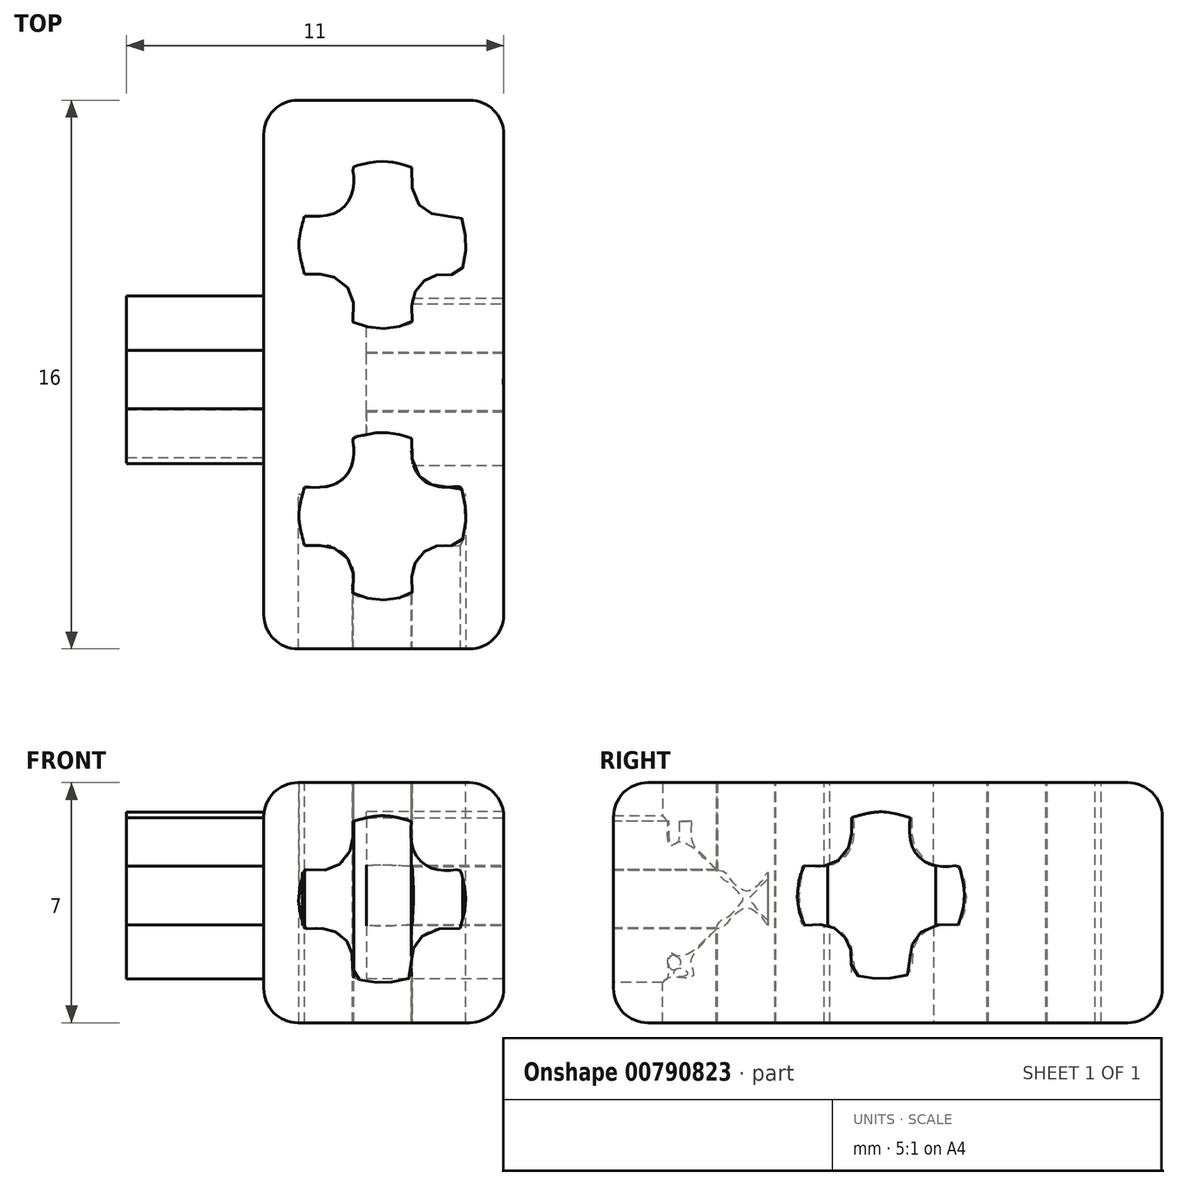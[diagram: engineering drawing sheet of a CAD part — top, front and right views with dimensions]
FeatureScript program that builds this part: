
annotation { "Feature Type Name" : "Feature", "Feature Type Description" : "" }
export const myFeature = defineFeature(function(context is Context, id is Id, definition is map)
    precondition{}
    {
        {
            var Q0;
            Q0=qCreatedBy(makeId("Top.planeOp"),FACE);
            var sketch = newSketch(context, id + "F0", { "sketchPlane" : qUnion([Q0])});
            skLineSegment(sketch, "E0.bottom", {"start": v(-3.5, 8) * mm, "end": v(3.5, 8) * mm});
            skLineSegment(sketch, "E0.top", {"start": v(-3.5, -8) * mm, "end": v(3.5, -8) * mm});
            skLineSegment(sketch, "E0.left", {"start": v(-3.5, 8) * mm, "end": v(-3.5, -8) * mm});
            skLineSegment(sketch, "E0.right", {"start": v(3.5, 8) * mm, "end": v(3.5, -8) * mm});
            skPoint(sketch, "E1", {"position": v(0, 8) * mm});
            skPoint(sketch, "E2", {"position": v(-3.5, 0) * mm});
            skSolve(sketch);
        }
        {
            var Q0;
            Q0=makeQuery(id+"F0.imprint","IMPRINT",FACE,{"disambiguationData":[TD([[makeQuery(id+"F0.imprint","IMPRINT",EDGE,{"derivedFrom":sQuery(id+"F0.wireOp",EDGE,"E0.bottom")}),-1.0]])]});
            extrude(context, id + "F1", {"entities" : qUnion([Q0]), "depth" : 7 * mm, "offsetDistance" : 25 * mm});
        }
        {
            var Q0;
            Q0=makeQuery(id+"F1.opExtrude","SWEPT_FACE",FACE,{"disambiguationData":[OSD([sQuery(id+"F0.wireOp",EDGE,"E0.left")])]});
            var sketch = newSketch(context, id + "F2", { "sketchPlane" : qUnion([Q0])});
            skFitSpline(sketch, "E3", {"points": [v(-0.7, 5.97) * mm, v(0.18, 6.14) * mm, v(1, 5.97) * mm], "startDerivative": vector(1.75, 0.5) * mm, "endDerivative": vector(1.65, -0.5) * mm});
            skFitSpline(sketch, "E4", {"points": [v(1, 5.97) * mm, v(1, 5.4) * mm, v(1.15, 4.97) * mm, v(1.46, 4.67) * mm, v(1.8, 4.56) * mm, v(2.22, 4.55) * mm, v(2.42, 4.55) * mm, v(2.5, 4.3) * mm, v(2.58, 3.92) * mm, v(2.59, 3.58) * mm, v(2.54, 3.26) * mm, v(2.42, 2.85) * mm], "startDerivative": vector(-0.26, -5.18) * mm, "endDerivative": vector(-1.41, -4.37) * mm});
            skFitSpline(sketch, "E5", {"points": [v(-0.7, 5.97) * mm, v(-0.7, 5.68) * mm, v(-0.7, 5.43) * mm, v(-0.73, 5.24) * mm, v(-0.9, 4.9) * mm, v(-1.1, 4.72) * mm, v(-1.36, 4.6) * mm, v(-1.68, 4.55) * mm, v(-2.12, 4.55) * mm, v(-2.21, 4.27) * mm, v(-2.27, 3.98) * mm, v(-2.29, 3.66) * mm, v(-2.26, 3.37) * mm, v(-2.2, 3.1) * mm, v(-2.12, 2.85) * mm, v(-1.93, 2.85) * mm, v(-1.61, 2.85) * mm, v(-1.36, 2.81) * mm, v(-1.17, 2.73) * mm, v(-0.95, 2.56) * mm, v(-0.84, 2.42) * mm, v(-0.76, 2.24) * mm, v(-0.7, 2) * mm, v(-0.7, 1.75) * mm, v(-0.7, 1.43) * mm, v(-0.44, 1.35) * mm, v(-0.1, 1.29) * mm, v(0.18, 1.28) * mm, v(0.45, 1.3) * mm, v(0.82, 1.37) * mm, v(1, 1.43) * mm, v(1, 1.75) * mm, v(1, 2.03) * mm, v(1.1, 2.35) * mm, v(1.24, 2.55) * mm, v(1.5, 2.75) * mm, v(1.92, 2.85) * mm, v(2.42, 2.85) * mm], "startDerivative": vector(-0.02, -10.87) * mm, "endDerivative": vector(14.17, -0.52) * mm});
            skSolve(sketch);
        }
        {
            var Q0;
            Q0=makeQuery(id+"F2.imprint","IMPRINT",FACE,{"disambiguationData":[TD([[makeQuery(id+"F2.imprint","IMPRINT",EDGE,{"derivedFrom":sQuery(id+"F2.wireOp",EDGE,"E3")}),-1.0]])]});
            var Q1;
            Q1=makeQuery(id+"F2.imprint","IMPRINT",FACE,{"disambiguationData":[TD([[makeQuery(id+"F2.imprint","IMPRINT",EDGE,{"derivedFrom":sQuery(id+"F2.wireOp",EDGE,"d630b020-bbd6-4e47-9868-e03ddda9818e")}),-1.0]])]});
            extrude(context, id + "F3", {"entities" : qUnion([Q0, Q1]), "depth" : 4 * mm, "offsetDistance" : 25 * mm});
        }
        {
            var Q0;
            Q0=makeQuery(id+"F1.opExtrude","SWEPT_FACE",FACE,{"disambiguationData":[OSD([sQuery(id+"F0.wireOp",EDGE,"E0.top")])]});
            var sketch = newSketch(context, id + "F4", { "sketchPlane" : qUnion([Q0])});
            skFitSpline(sketch, "E6", {"points": [v(-0.9, 5.87) * mm, v(-0.02, 6.04) * mm, v(0.8, 5.87) * mm], "startDerivative": vector(1.75, 0.5) * mm, "endDerivative": vector(1.65, -0.5) * mm});
            skFitSpline(sketch, "E7", {"points": [v(0.8, 5.87) * mm, v(0.8, 5.3) * mm, v(0.95, 4.87) * mm, v(1.26, 4.57) * mm, v(1.6, 4.46) * mm, v(2.02, 4.45) * mm, v(2.22, 4.45) * mm, v(2.3, 4.2) * mm, v(2.38, 3.82) * mm, v(2.39, 3.48) * mm, v(2.34, 3.16) * mm, v(2.22, 2.75) * mm], "startDerivative": vector(-0.26, -5.18) * mm, "endDerivative": vector(-1.41, -4.37) * mm});
            skFitSpline(sketch, "E8", {"points": [v(-0.9, 5.87) * mm, v(-0.9, 5.58) * mm, v(-0.9, 5.33) * mm, v(-0.93, 5.14) * mm, v(-1.1, 4.8) * mm, v(-1.3, 4.61) * mm, v(-1.56, 4.49) * mm, v(-1.88, 4.45) * mm, v(-2.32, 4.45) * mm, v(-2.41, 4.17) * mm, v(-2.47, 3.88) * mm, v(-2.49, 3.55) * mm, v(-2.46, 3.27) * mm, v(-2.4, 3) * mm, v(-2.32, 2.75) * mm, v(-2.13, 2.75) * mm, v(-1.81, 2.75) * mm, v(-1.56, 2.71) * mm, v(-1.37, 2.63) * mm, v(-1.15, 2.46) * mm, v(-1.04, 2.32) * mm, v(-0.96, 2.14) * mm, v(-0.9, 1.9) * mm, v(-0.9, 1.65) * mm, v(-0.9, 1.33) * mm, v(-0.64, 1.25) * mm, v(-0.3, 1.19) * mm, v(-0.02, 1.18) * mm, v(0.25, 1.2) * mm, v(0.62, 1.27) * mm, v(0.8, 1.33) * mm, v(0.8, 1.65) * mm, v(0.8, 1.92) * mm, v(0.9, 2.25) * mm, v(1.04, 2.45) * mm, v(1.3, 2.65) * mm, v(1.72, 2.75) * mm, v(2.22, 2.75) * mm], "startDerivative": vector(-0.02, -10.87) * mm, "endDerivative": vector(14.17, -0.52) * mm});
            skFitSpline(sketch, "E9", {"points": [v(9.4, 6.1) * mm, v(10.29, 6.27) * mm, v(11.1, 6.1) * mm], "startDerivative": vector(1.75, 0.5) * mm, "endDerivative": vector(1.65, -0.5) * mm});
            skFitSpline(sketch, "E10", {"points": [v(11.1, 6.1) * mm, v(11.1, 5.54) * mm, v(11.25, 5.1) * mm, v(11.57, 4.8) * mm, v(11.9, 4.7) * mm, v(12.32, 4.68) * mm, v(12.52, 4.68) * mm, v(12.6, 4.44) * mm, v(12.68, 4.05) * mm, v(12.69, 3.71) * mm, v(12.65, 3.4) * mm, v(12.52, 2.98) * mm], "startDerivative": vector(-0.26, -5.18) * mm, "endDerivative": vector(-1.41, -4.37) * mm});
            skFitSpline(sketch, "E11", {"points": [v(9.4, 6.1) * mm, v(9.4, 5.8) * mm, v(9.4, 5.56) * mm, v(9.37, 5.37) * mm, v(9.2, 5.03) * mm, v(9, 4.85) * mm, v(8.74, 4.72) * mm, v(8.42, 4.68) * mm, v(7.98, 4.68) * mm, v(7.9, 4.4) * mm, v(7.83, 4.12) * mm, v(7.81, 3.79) * mm, v(7.84, 3.5) * mm, v(7.9, 3.23) * mm, v(7.98, 2.98) * mm, v(8.18, 2.98) * mm, v(8.5, 2.98) * mm, v(8.74, 2.95) * mm, v(8.93, 2.87) * mm, v(9.15, 2.7) * mm, v(9.26, 2.55) * mm, v(9.35, 2.37) * mm, v(9.4, 2.13) * mm, v(9.4, 1.88) * mm, v(9.4, 1.56) * mm, v(9.66, 1.48) * mm, v(10, 1.42) * mm, v(10.29, 1.4) * mm, v(10.55, 1.43) * mm, v(10.92, 1.5) * mm, v(11.1, 1.56) * mm, v(11.1, 1.88) * mm, v(11.1, 2.16) * mm, v(11.2, 2.49) * mm, v(11.34, 2.68) * mm, v(11.61, 2.88) * mm, v(12.03, 2.98) * mm, v(12.52, 2.98) * mm], "startDerivative": vector(-0.02, -10.87) * mm, "endDerivative": vector(14.17, -0.52) * mm});
            skFitSpline(sketch, "E12", {"points": [v(18.93, 6.02) * mm, v(19.82, 6.2) * mm, v(20.63, 6.02) * mm], "startDerivative": vector(1.75, 0.5) * mm, "endDerivative": vector(1.65, -0.5) * mm});
            skFitSpline(sketch, "E13", {"points": [v(20.63, 6.02) * mm, v(20.64, 5.46) * mm, v(20.78, 5.03) * mm, v(21.1, 4.73) * mm, v(21.44, 4.61) * mm, v(21.85, 4.6) * mm, v(22.05, 4.6) * mm, v(22.13, 4.36) * mm, v(22.2, 3.98) * mm, v(22.22, 3.64) * mm, v(22.18, 3.32) * mm, v(22.05, 2.9) * mm], "startDerivative": vector(-0.26, -5.18) * mm, "endDerivative": vector(-1.41, -4.37) * mm});
            skFitSpline(sketch, "E14", {"points": [v(18.93, 6.02) * mm, v(18.93, 5.73) * mm, v(18.93, 5.48) * mm, v(18.9, 5.3) * mm, v(18.73, 4.95) * mm, v(18.53, 4.77) * mm, v(18.27, 4.64) * mm, v(17.95, 4.6) * mm, v(17.51, 4.6) * mm, v(17.42, 4.32) * mm, v(17.37, 4.04) * mm, v(17.35, 3.7) * mm, v(17.37, 3.42) * mm, v(17.43, 3.15) * mm, v(17.51, 2.9) * mm, v(17.7, 2.9) * mm, v(18.02, 2.9) * mm, v(18.27, 2.87) * mm, v(18.46, 2.79) * mm, v(18.68, 2.61) * mm, v(18.79, 2.47) * mm, v(18.88, 2.3) * mm, v(18.93, 2.05) * mm, v(18.93, 1.8) * mm, v(18.93, 1.48) * mm, v(19.2, 1.4) * mm, v(19.54, 1.34) * mm, v(19.82, 1.33) * mm, v(20.08, 1.35) * mm, v(20.45, 1.42) * mm, v(20.63, 1.48) * mm, v(20.63, 1.8) * mm, v(20.64, 2.08) * mm, v(20.74, 2.4) * mm, v(20.88, 2.6) * mm, v(21.14, 2.8) * mm, v(21.56, 2.9) * mm, v(22.05, 2.9) * mm], "startDerivative": vector(-0.02, -10.87) * mm, "endDerivative": vector(14.17, -0.52) * mm});
            skSolve(sketch);
        }
        {
            var Q0;
            Q0=makeQuery(id+"F4.imprint","IMPRINT",FACE,{"disambiguationData":[TD([[makeQuery(id+"F4.imprint","IMPRINT",EDGE,{"derivedFrom":sQuery(id+"F4.wireOp",EDGE,"E6")}),-1.0]])]});
            extrude(context, id + "F5", {"entities" : qUnion([Q0]), "operationType" : NewBodyOperationType.REMOVE, "oppositeDirection" : true, "depth" : 4.5 * mm, "offsetDistance" : 25 * mm});
        }
        {
            var Q0;
            Q0=makeQuery(id+"F1.opExtrude","SWEPT_FACE",FACE,{"disambiguationData":[OSD([sQuery(id+"F0.wireOp",EDGE,"E0.right")])]});
            var sketch = newSketch(context, id + "F6", { "sketchPlane" : qUnion([Q0])});
            skFitSpline(sketch, "E15", {"points": [v(-1.06, 5.98) * mm, v(-0.18, 6.15) * mm, v(0.64, 5.98) * mm], "startDerivative": vector(1.75, 0.5) * mm, "endDerivative": vector(1.65, -0.5) * mm});
            skFitSpline(sketch, "E16", {"points": [v(0.64, 5.98) * mm, v(0.64, 5.42) * mm, v(0.79, 4.98) * mm, v(1.1, 4.68) * mm, v(1.44, 4.57) * mm, v(1.86, 4.56) * mm, v(2.06, 4.56) * mm, v(2.14, 4.32) * mm, v(2.21, 3.93) * mm, v(2.22, 3.6) * mm, v(2.18, 3.27) * mm, v(2.06, 2.86) * mm], "startDerivative": vector(-0.26, -5.18) * mm, "endDerivative": vector(-1.41, -4.37) * mm});
            skFitSpline(sketch, "E17", {"points": [v(-1.06, 5.98) * mm, v(-1.06, 5.69) * mm, v(-1.06, 5.44) * mm, v(-1.1, 5.25) * mm, v(-1.26, 4.9) * mm, v(-1.46, 4.73) * mm, v(-1.72, 4.6) * mm, v(-2.04, 4.56) * mm, v(-2.48, 4.56) * mm, v(-2.57, 4.28) * mm, v(-2.63, 4) * mm, v(-2.65, 3.67) * mm, v(-2.62, 3.38) * mm, v(-2.56, 3.11) * mm, v(-2.48, 2.86) * mm, v(-2.29, 2.86) * mm, v(-1.97, 2.86) * mm, v(-1.73, 2.82) * mm, v(-1.54, 2.74) * mm, v(-1.31, 2.57) * mm, v(-1.2, 2.43) * mm, v(-1.12, 2.25) * mm, v(-1.06, 2) * mm, v(-1.06, 1.76) * mm, v(-1.06, 1.44) * mm, v(-0.8, 1.36) * mm, v(-0.46, 1.3) * mm, v(-0.18, 1.29) * mm, v(0.09, 1.3) * mm, v(0.45, 1.38) * mm, v(0.64, 1.44) * mm, v(0.64, 1.76) * mm, v(0.64, 2.04) * mm, v(0.74, 2.36) * mm, v(0.88, 2.56) * mm, v(1.15, 2.76) * mm, v(1.56, 2.86) * mm, v(2.06, 2.86) * mm], "startDerivative": vector(-0.02, -10.87) * mm, "endDerivative": vector(14.17, -0.52) * mm});
            skSolve(sketch);
        }
        {
            var Q0;
            Q0=makeQuery(id+"F6.imprint","IMPRINT",FACE,{"disambiguationData":[TD([[makeQuery(id+"F6.imprint","IMPRINT",EDGE,{"derivedFrom":sQuery(id+"F6.wireOp",EDGE,"E15")}),-1.0]])]});
            extrude(context, id + "F7", {"entities" : qUnion([Q0]), "operationType" : NewBodyOperationType.REMOVE, "oppositeDirection" : true, "depth" : 4 * mm, "offsetDistance" : 25 * mm});
        }
        {
            var Q0;
            Q0=makeQuery(id+"F1.opExtrude","CAP_FACE",FACE,{"disambiguationData":[OSD([sQuery(id+"F0.wireOp",EDGE,"E0.bottom"),sQuery(id+"F0.wireOp",EDGE,"E0.top"),sQuery(id+"F0.wireOp",EDGE,"E0.left"),sQuery(id+"F0.wireOp",EDGE,"E0.right")])],"isStart":false});
            var sketch = newSketch(context, id + "F8", { "sketchPlane" : qUnion([Q0])});
            skFitSpline(sketch, "E18", {"points": [v(-2.3, -4.98) * mm, v(-2.47, -4.1) * mm, v(-2.3, -3.28) * mm], "startDerivative": vector(-0.5, 1.75) * mm, "endDerivative": vector(0.5, 1.65) * mm});
            skFitSpline(sketch, "E19", {"points": [v(-2.3, -3.28) * mm, v(-1.74, -3.28) * mm, v(-1.3, -3.13) * mm, v(-1, -2.82) * mm, v(-0.9, -2.48) * mm, v(-0.89, -2.06) * mm, v(-0.89, -1.86) * mm, v(-0.64, -1.78) * mm, v(-0.26, -1.7) * mm, v(0.08, -1.7) * mm, v(0.4, -1.74) * mm, v(0.81, -1.86) * mm], "startDerivative": vector(5.18, -0.26) * mm, "endDerivative": vector(4.37, -1.41) * mm});
            skFitSpline(sketch, "E20", {"points": [v(-2.3, -4.98) * mm, v(-2.01, -4.98) * mm, v(-1.76, -4.98) * mm, v(-1.57, -5.01) * mm, v(-1.23, -5.18) * mm, v(-1.05, -5.38) * mm, v(-0.92, -5.64) * mm, v(-0.89, -5.96) * mm, v(-0.89, -6.4) * mm, v(-0.6, -6.5) * mm, v(-0.32, -6.55) * mm, v(0.01, -6.57) * mm, v(0.3, -6.54) * mm, v(0.56, -6.48) * mm, v(0.81, -6.4) * mm, v(0.81, -6.2) * mm, v(0.82, -5.9) * mm, v(0.85, -5.65) * mm, v(0.93, -5.46) * mm, v(1.1, -5.23) * mm, v(1.24, -5.12) * mm, v(1.42, -5.04) * mm, v(1.67, -4.98) * mm, v(1.92, -4.98) * mm, v(2.24, -4.98) * mm, v(2.32, -4.72) * mm, v(2.38, -4.38) * mm, v(2.39, -4.1) * mm, v(2.37, -3.83) * mm, v(2.3, -3.47) * mm, v(2.24, -3.28) * mm, v(1.92, -3.28) * mm, v(1.64, -3.28) * mm, v(1.31, -3.18) * mm, v(1.12, -3.04) * mm, v(0.91, -2.77) * mm, v(0.81, -2.36) * mm, v(0.81, -1.86) * mm], "startDerivative": vector(10.87, -0.02) * mm, "endDerivative": vector(0.52, 14.17) * mm});
            skFitSpline(sketch, "E21", {"points": [v(-2.3, 2.92) * mm, v(-2.47, 3.8) * mm, v(-2.3, 4.62) * mm], "startDerivative": vector(-0.5, 1.75) * mm, "endDerivative": vector(0.5, 1.65) * mm});
            skFitSpline(sketch, "E22", {"points": [v(-2.3, 4.62) * mm, v(-1.74, 4.62) * mm, v(-1.3, 4.77) * mm, v(-1, 5.08) * mm, v(-0.9, 5.43) * mm, v(-0.89, 5.84) * mm, v(-0.89, 6.04) * mm, v(-0.64, 6.12) * mm, v(-0.26, 6.2) * mm, v(0.08, 6.2) * mm, v(0.4, 6.16) * mm, v(0.81, 6.04) * mm], "startDerivative": vector(5.18, -0.26) * mm, "endDerivative": vector(4.37, -1.41) * mm});
            skFitSpline(sketch, "E23", {"points": [v(-2.3, 2.92) * mm, v(-2.01, 2.92) * mm, v(-1.76, 2.92) * mm, v(-1.57, 2.9) * mm, v(-1.23, 2.72) * mm, v(-1.05, 2.52) * mm, v(-0.92, 2.26) * mm, v(-0.89, 1.94) * mm, v(-0.89, 1.5) * mm, v(-0.6, 1.41) * mm, v(-0.32, 1.35) * mm, v(0.01, 1.33) * mm, v(0.3, 1.36) * mm, v(0.56, 1.42) * mm, v(0.81, 1.5) * mm, v(0.81, 1.7) * mm, v(0.82, 2) * mm, v(0.85, 2.26) * mm, v(0.93, 2.45) * mm, v(1.1, 2.67) * mm, v(1.24, 2.78) * mm, v(1.42, 2.87) * mm, v(1.67, 2.92) * mm, v(1.92, 2.92) * mm, v(2.24, 2.92) * mm, v(2.32, 3.18) * mm, v(2.38, 3.53) * mm, v(2.39, 3.8) * mm, v(2.37, 4.07) * mm, v(2.3, 4.44) * mm, v(2.24, 4.62) * mm, v(1.92, 4.62) * mm, v(1.64, 4.63) * mm, v(1.31, 4.73) * mm, v(1.12, 4.86) * mm, v(0.91, 5.13) * mm, v(0.81, 5.55) * mm, v(0.81, 6.04) * mm], "startDerivative": vector(10.87, -0.02) * mm, "endDerivative": vector(0.52, 14.17) * mm});
            skSolve(sketch);
        }
        {
            var Q0;
            Q0=makeQuery(id+"F8.imprint","IMPRINT",FACE,{"disambiguationData":[TD([[makeQuery(id+"F8.imprint","IMPRINT",EDGE,{"derivedFrom":sQuery(id+"F8.wireOp",EDGE,"E18")}),-1.0]])]});
            var Q1;
            Q1=makeQuery(id+"F8.imprint","IMPRINT",FACE,{"disambiguationData":[TD([[makeQuery(id+"F8.imprint","IMPRINT",EDGE,{"derivedFrom":sQuery(id+"F8.wireOp",EDGE,"E21")}),-1.0]])]});
            extrude(context, id + "F9", {"entities" : qUnion([Q0, Q1]), "operationType" : NewBodyOperationType.REMOVE, "oppositeDirection" : true, "depth" : 9.6 * mm, "offsetDistance" : 25 * mm});
        }
        {
            var Q0;
            Q0=makeQuery(id+"F1.opExtrude","CAP_EDGE",EDGE,{"disambiguationData":[OSD([sQuery(id+"F0.wireOp",EDGE,"E0.bottom")])],"isStart":false});
            var Q1;
            Q1=makeQuery(id+"F1.opExtrude","SWEPT_EDGE",EDGE,{"disambiguationData":[OSD([sQuery(id+"F0.wireOp",EDGE,"E0.bottom"),sQuery(id+"F0.wireOp",EDGE,"E0.left")])]});
            var Q2;
            Q2=makeQuery(id+"F1.opExtrude","CAP_EDGE",EDGE,{"disambiguationData":[OSD([sQuery(id+"F0.wireOp",EDGE,"E0.bottom")])],"isStart":true});
            var Q3;
            Q3=makeQuery(id+"F1.opExtrude","SWEPT_EDGE",EDGE,{"disambiguationData":[OSD([sQuery(id+"F0.wireOp",EDGE,"E0.bottom"),sQuery(id+"F0.wireOp",EDGE,"E0.right")])]});
            var Q4;
            Q4=makeQuery(id+"F1.opExtrude","CAP_EDGE",EDGE,{"disambiguationData":[OSD([sQuery(id+"F0.wireOp",EDGE,"E0.top")])],"isStart":false});
            var Q5;
            Q5=makeQuery(id+"F1.opExtrude","SWEPT_EDGE",EDGE,{"disambiguationData":[OSD([sQuery(id+"F0.wireOp",EDGE,"E0.top"),sQuery(id+"F0.wireOp",EDGE,"E0.left")])]});
            var Q6;
            Q6=makeQuery(id+"F1.opExtrude","CAP_EDGE",EDGE,{"disambiguationData":[OSD([sQuery(id+"F0.wireOp",EDGE,"E0.top")])],"isStart":true});
            var Q7;
            Q7=makeQuery(id+"F1.opExtrude","SWEPT_EDGE",EDGE,{"disambiguationData":[OSD([sQuery(id+"F0.wireOp",EDGE,"E0.top"),sQuery(id+"F0.wireOp",EDGE,"E0.right")])]});
            fillet(context, id + "F10", {"entities" : qUnion([Q0, Q1, Q2, Q3, Q4, Q5, Q6, Q7]), "radius" : 1 * mm, "tangentPropagation" : true, "allowEdgeOverflow" : false});
        }
        {
            var Q0;
            Q0=makeQuery(id+"F1.opExtrude","CAP_EDGE",EDGE,{"disambiguationData":[OSD([sQuery(id+"F0.wireOp",EDGE,"E0.left")])],"isStart":false});
            var Q1;
            {var subQ0=sQuery(id+"F0.wireOp",EDGE,"E0.bottom");Q1=makeQuery(id+"F10.opFillet","BLEND_EDGE",EDGE,{"blendedFrom":[makeQuery(id+"F1.opExtrude","SWEPT_EDGE",EDGE,{"disambiguationData":[OSD([subQ0,sQuery(id+"F0.wireOp",EDGE,"E0.right")])]}),makeQuery(id+"F1.opExtrude","CAP_EDGE",EDGE,{"disambiguationData":[OSD([subQ0])],"isStart":false})],"blendedInto":[]});}
            var Q2;
            Q2=makeQuery(id+"F1.opExtrude","CAP_EDGE",EDGE,{"disambiguationData":[OSD([sQuery(id+"F0.wireOp",EDGE,"E0.right")])],"isStart":false});
            var Q3;
            {var subQ0=sQuery(id+"F0.wireOp",EDGE,"E0.top");Q3=makeQuery(id+"F10.opFillet","BLEND_EDGE",EDGE,{"blendedFrom":[makeQuery(id+"F1.opExtrude","SWEPT_EDGE",EDGE,{"disambiguationData":[OSD([subQ0,sQuery(id+"F0.wireOp",EDGE,"E0.left")])]}),makeQuery(id+"F1.opExtrude","CAP_EDGE",EDGE,{"disambiguationData":[OSD([subQ0])],"isStart":false})],"blendedInto":[]});}
            var Q4;
            {var subQ0=sQuery(id+"F0.wireOp",EDGE,"E0.top");Q4=makeQuery(id+"F10.opFillet","BLEND_EDGE",EDGE,{"blendedFrom":[makeQuery(id+"F1.opExtrude","SWEPT_EDGE",EDGE,{"disambiguationData":[OSD([subQ0,sQuery(id+"F0.wireOp",EDGE,"E0.right")])]}),makeQuery(id+"F1.opExtrude","CAP_EDGE",EDGE,{"disambiguationData":[OSD([subQ0])],"isStart":false})],"blendedInto":[]});}
            var Q5;
            {var subQ0=sQuery(id+"F0.wireOp",EDGE,"E0.bottom");Q5=makeQuery(id+"F10.opFillet","BLEND_EDGE",EDGE,{"blendedFrom":[makeQuery(id+"F1.opExtrude","SWEPT_EDGE",EDGE,{"disambiguationData":[OSD([subQ0,sQuery(id+"F0.wireOp",EDGE,"E0.left")])]}),makeQuery(id+"F1.opExtrude","CAP_EDGE",EDGE,{"disambiguationData":[OSD([subQ0])],"isStart":true})],"blendedInto":[]});}
            var Q6;
            Q6=makeQuery(id+"F1.opExtrude","CAP_EDGE",EDGE,{"disambiguationData":[OSD([sQuery(id+"F0.wireOp",EDGE,"E0.left")])],"isStart":true});
            var Q7;
            {var subQ0=sQuery(id+"F0.wireOp",EDGE,"E0.top");Q7=makeQuery(id+"F10.opFillet","BLEND_EDGE",EDGE,{"blendedFrom":[makeQuery(id+"F1.opExtrude","SWEPT_EDGE",EDGE,{"disambiguationData":[OSD([subQ0,sQuery(id+"F0.wireOp",EDGE,"E0.left")])]}),makeQuery(id+"F1.opExtrude","CAP_EDGE",EDGE,{"disambiguationData":[OSD([subQ0])],"isStart":true})],"blendedInto":[]});}
            var Q8;
            {var subQ0=sQuery(id+"F0.wireOp",EDGE,"E0.bottom");Q8=makeQuery(id+"F10.opFillet","BLEND_EDGE",EDGE,{"blendedFrom":[makeQuery(id+"F1.opExtrude","SWEPT_EDGE",EDGE,{"disambiguationData":[OSD([subQ0,sQuery(id+"F0.wireOp",EDGE,"E0.right")])]}),makeQuery(id+"F1.opExtrude","CAP_EDGE",EDGE,{"disambiguationData":[OSD([subQ0])],"isStart":true})],"blendedInto":[]});}
            var Q9;
            Q9=makeQuery(id+"F1.opExtrude","CAP_EDGE",EDGE,{"disambiguationData":[OSD([sQuery(id+"F0.wireOp",EDGE,"E0.right")])],"isStart":true});
            var Q10;
            {var subQ0=sQuery(id+"F0.wireOp",EDGE,"E0.top");Q10=makeQuery(id+"F10.opFillet","BLEND_EDGE",EDGE,{"blendedFrom":[makeQuery(id+"F1.opExtrude","SWEPT_EDGE",EDGE,{"disambiguationData":[OSD([subQ0,sQuery(id+"F0.wireOp",EDGE,"E0.right")])]}),makeQuery(id+"F1.opExtrude","CAP_EDGE",EDGE,{"disambiguationData":[OSD([subQ0])],"isStart":true})],"blendedInto":[]});}
            fillet(context, id + "F11", {"entities" : qUnion([Q0, Q1, Q2, Q3, Q4, Q5, Q6, Q7, Q8, Q9, Q10]), "radius" : 1 * mm, "tangentPropagation" : true, "allowEdgeOverflow" : false});
        }
    });
